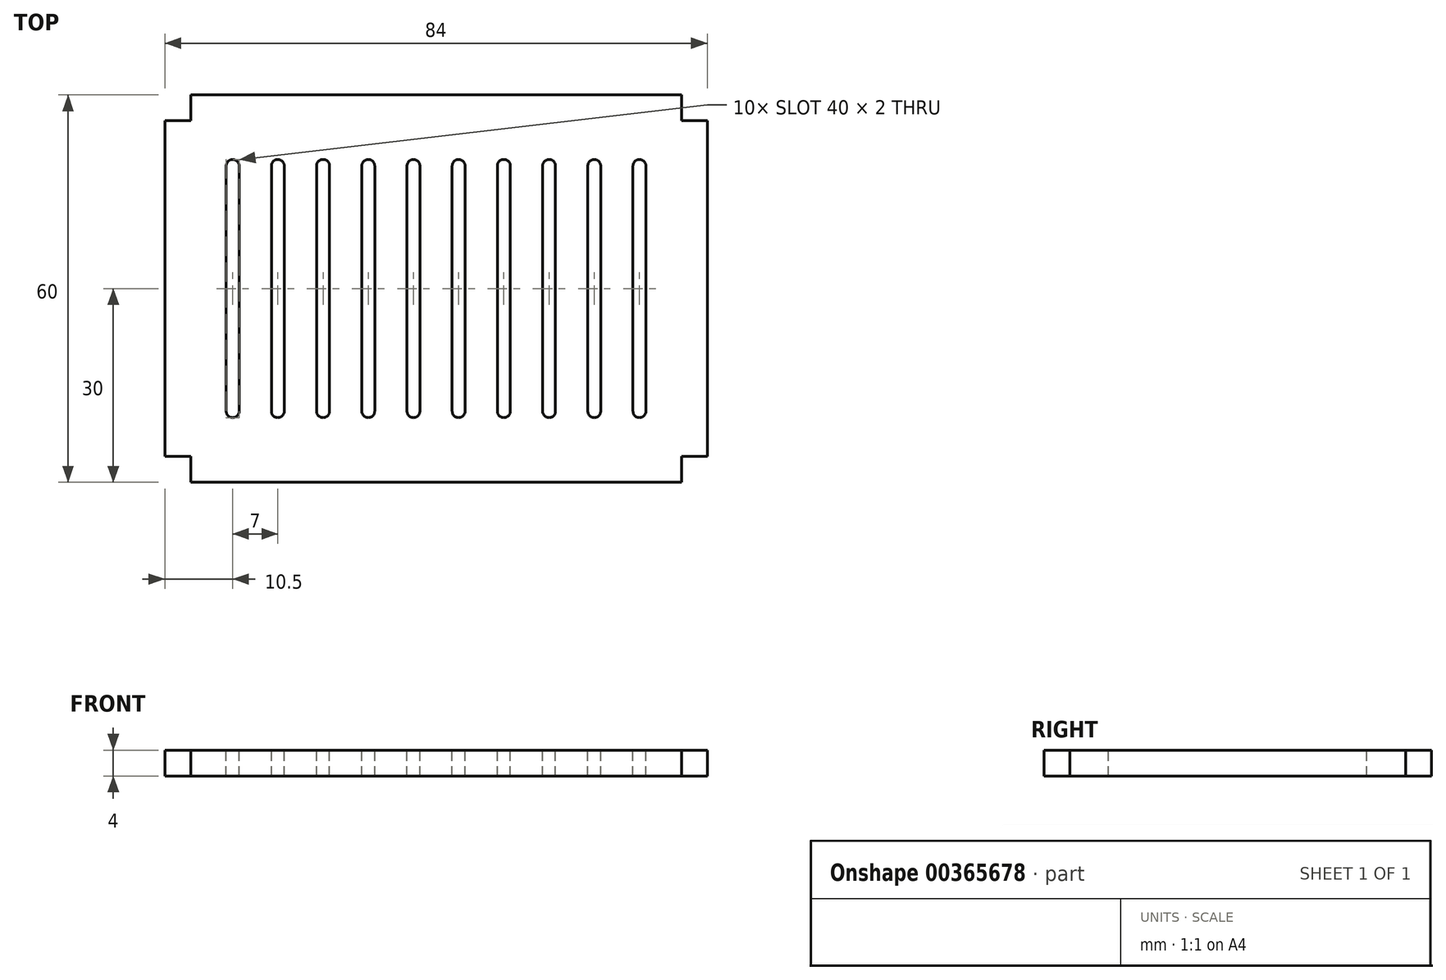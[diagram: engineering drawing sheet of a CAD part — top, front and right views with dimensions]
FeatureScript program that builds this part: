
annotation { "Feature Type Name" : "Feature", "Feature Type Description" : "" }
export const myFeature = defineFeature(function(context is Context, id is Id, definition is map)
    precondition{}
    {
        {
            var Q0;
            Q0=qCreatedBy(makeId("Top.planeOp"),FACE);
            var sketch = newSketch(context, id + "F0", { "sketchPlane" : qUnion([Q0])});
            skLineSegment(sketch, "E0.bottom", {"start": v(0, 0) * mm, "end": v(84, 0) * mm});
            skLineSegment(sketch, "E0.top", {"start": v(0, 60) * mm, "end": v(84, 60) * mm});
            skLineSegment(sketch, "E0.left", {"start": v(0, 0) * mm, "end": v(0, 60) * mm});
            skLineSegment(sketch, "E0.right", {"start": v(84, 0) * mm, "end": v(84, 60) * mm});
            skSolve(sketch);
        }
        {
            var Q0;
            Q0 = qSketchRegion(id + "F0", true);
            extrude(context, id + "F1", {"entities" : qUnion([Q0]), "depth" : 4 * mm});
        }
        {
            var Q0;
            Q0=makeQuery(id+"F1.opExtrude","CAP_FACE",FACE,{"disambiguationData":[OSD([sQuery(id+"F0.wireOp",EDGE,"E0.bottom"),sQuery(id+"F0.wireOp",EDGE,"E0.top"),sQuery(id+"F0.wireOp",EDGE,"E0.left"),sQuery(id+"F0.wireOp",EDGE,"E0.right")])],"isStart":false});
            var sketch = newSketch(context, id + "F2", { "sketchPlane" : qUnion([Q0])});
            skLineSegment(sketch, "E1.bottom", {"start": v(0, 0) * mm, "end": v(4, 0) * mm});
            skLineSegment(sketch, "E1.top", {"start": v(0, 4) * mm, "end": v(4, 4) * mm});
            skLineSegment(sketch, "E1.left", {"start": v(0, 0) * mm, "end": v(0, 4) * mm});
            skLineSegment(sketch, "E1.right", {"start": v(4, 0) * mm, "end": v(4, 4) * mm});
            skLineSegment(sketch, "E2.0.1.0", {"start": v(0, 56) * mm, "end": v(4, 56) * mm});
            skLineSegment(sketch, "E2.0.1.1", {"start": v(0, 60) * mm, "end": v(4, 60) * mm});
            skLineSegment(sketch, "E2.0.1.2", {"start": v(0, 56) * mm, "end": v(0, 60) * mm});
            skLineSegment(sketch, "E2.0.1.3", {"start": v(4, 56) * mm, "end": v(4, 60) * mm});
            skLineSegment(sketch, "E2.1.0.0", {"start": v(80, 0) * mm, "end": v(84, 0) * mm});
            skLineSegment(sketch, "E2.1.0.1", {"start": v(80, 4) * mm, "end": v(84, 4) * mm});
            skLineSegment(sketch, "E2.1.0.2", {"start": v(80, 0) * mm, "end": v(80, 4) * mm});
            skLineSegment(sketch, "E2.1.0.3", {"start": v(84, 0) * mm, "end": v(84, 4) * mm});
            skLineSegment(sketch, "E2.1.1.0", {"start": v(80, 56) * mm, "end": v(84, 56) * mm});
            skLineSegment(sketch, "E2.1.1.1", {"start": v(80, 60) * mm, "end": v(84, 60) * mm});
            skLineSegment(sketch, "E2.1.1.2", {"start": v(80, 56) * mm, "end": v(80, 60) * mm});
            skLineSegment(sketch, "E2.1.1.3", {"start": v(84, 56) * mm, "end": v(84, 60) * mm});
            skLineSegment(sketch, "E2.direction1", {"start": v(0, 0) * mm, "end": v(80, 0) * mm, "construction": true});
            skLineSegment(sketch, "E2.direction2", {"start": v(0, 0) * mm, "end": v(0, 56) * mm, "construction": true});
            skSolve(sketch);
        }
        {
            var Q0;
            Q0 = qSketchRegion(id + "F2", true);
            extrude(context, id + "F3", {"entities" : qUnion([Q0]), "operationType" : NewBodyOperationType.REMOVE, "endBound" : BoundingType.UP_TO_NEXT, "oppositeDirection" : true, "depth" : 25 * mm});
        }
        {
            var Q0;
            Q0=makeQuery(id+"F1.opExtrude","CAP_FACE",FACE,{"disambiguationData":[OSD([sQuery(id+"F0.wireOp",EDGE,"E0.bottom"),sQuery(id+"F0.wireOp",EDGE,"E0.top"),sQuery(id+"F0.wireOp",EDGE,"E0.left"),sQuery(id+"F0.wireOp",EDGE,"E0.right")])],"isStart":false});
            var sketch = newSketch(context, id + "F4", { "sketchPlane" : qUnion([Q0])});
            skLineSegment(sketch, "E3.bottom", {"start": v(10.5, 50) * mm, "end": v(10.5, 50) * mm});
            skLineSegment(sketch, "E3.top", {"start": v(10.5, 10) * mm, "end": v(10.5, 10) * mm});
            skLineSegment(sketch, "E3.left", {"start": v(9.5, 49) * mm, "end": v(9.5, 11) * mm});
            skLineSegment(sketch, "E3.right", {"start": v(11.5, 49) * mm, "end": v(11.5, 11) * mm});
            skPoint(sketch, "E4.visualSharp", {"position": v(9.5, 50) * mm});
            skArc(sketch, "E4.filletArc", {"start": v(10.5, 50) * mm, "mid": v(9.8, 49.7) * mm, "end": v(9.5, 49) * mm});
            skArc(sketch, "E5.filletArc", {"start": v(11.5, 49) * mm, "mid": v(11.2, 49.7) * mm, "end": v(10.5, 50) * mm});
            skPoint(sketch, "E6.visualSharp", {"position": v(11.5, 10) * mm});
            skArc(sketch, "E6.filletArc", {"start": v(10.5, 10) * mm, "mid": v(11.2, 10.3) * mm, "end": v(11.5, 11) * mm});
            skPoint(sketch, "E7.visualSharp", {"position": v(9.5, 10) * mm});
            skArc(sketch, "E7.filletArc", {"start": v(9.5, 11) * mm, "mid": v(9.8, 10.3) * mm, "end": v(10.5, 10) * mm});
            skPoint(sketch, "E8.1.0.0", {"position": v(16.5, 50) * mm});
            skLineSegment(sketch, "E8.1.0.1", {"start": v(16.5, 49) * mm, "end": v(16.5, 11) * mm});
            skLineSegment(sketch, "E8.1.0.2", {"start": v(18.5, 49) * mm, "end": v(18.5, 11) * mm});
            skPoint(sketch, "E8.1.0.3", {"position": v(18.5, 10) * mm});
            skPoint(sketch, "E8.1.0.4", {"position": v(16.5, 10) * mm});
            skArc(sketch, "E8.1.0.5", {"start": v(17.5, 10) * mm, "mid": v(18.2, 10.3) * mm, "end": v(18.5, 11) * mm});
            skArc(sketch, "E8.1.0.6", {"start": v(17.5, 50) * mm, "mid": v(16.8, 49.7) * mm, "end": v(16.5, 49) * mm});
            skArc(sketch, "E8.1.0.7", {"start": v(16.5, 11) * mm, "mid": v(16.8, 10.3) * mm, "end": v(17.5, 10) * mm});
            skArc(sketch, "E8.1.0.8", {"start": v(18.5, 49) * mm, "mid": v(18.2, 49.7) * mm, "end": v(17.5, 50) * mm});
            skPoint(sketch, "E8.2.0.0", {"position": v(23.5, 50) * mm});
            skLineSegment(sketch, "E8.2.0.1", {"start": v(23.5, 49) * mm, "end": v(23.5, 11) * mm});
            skLineSegment(sketch, "E8.2.0.2", {"start": v(25.5, 49) * mm, "end": v(25.5, 11) * mm});
            skPoint(sketch, "E8.2.0.3", {"position": v(25.5, 10) * mm});
            skPoint(sketch, "E8.2.0.4", {"position": v(23.5, 10) * mm});
            skArc(sketch, "E8.2.0.5", {"start": v(24.5, 10) * mm, "mid": v(25.2, 10.3) * mm, "end": v(25.5, 11) * mm});
            skArc(sketch, "E8.2.0.6", {"start": v(24.5, 50) * mm, "mid": v(23.8, 49.7) * mm, "end": v(23.5, 49) * mm});
            skArc(sketch, "E8.2.0.7", {"start": v(23.5, 11) * mm, "mid": v(23.8, 10.3) * mm, "end": v(24.5, 10) * mm});
            skArc(sketch, "E8.2.0.8", {"start": v(25.5, 49) * mm, "mid": v(25.2, 49.7) * mm, "end": v(24.5, 50) * mm});
            skPoint(sketch, "E8.3.0.0", {"position": v(30.5, 50) * mm});
            skLineSegment(sketch, "E8.3.0.1", {"start": v(30.5, 49) * mm, "end": v(30.5, 11) * mm});
            skLineSegment(sketch, "E8.3.0.2", {"start": v(32.5, 49) * mm, "end": v(32.5, 11) * mm});
            skPoint(sketch, "E8.3.0.3", {"position": v(32.5, 10) * mm});
            skPoint(sketch, "E8.3.0.4", {"position": v(30.5, 10) * mm});
            skArc(sketch, "E8.3.0.5", {"start": v(31.5, 10) * mm, "mid": v(32.2, 10.3) * mm, "end": v(32.5, 11) * mm});
            skArc(sketch, "E8.3.0.6", {"start": v(31.5, 50) * mm, "mid": v(30.8, 49.7) * mm, "end": v(30.5, 49) * mm});
            skArc(sketch, "E8.3.0.7", {"start": v(30.5, 11) * mm, "mid": v(30.8, 10.3) * mm, "end": v(31.5, 10) * mm});
            skArc(sketch, "E8.3.0.8", {"start": v(32.5, 49) * mm, "mid": v(32.2, 49.7) * mm, "end": v(31.5, 50) * mm});
            skPoint(sketch, "E8.4.0.0", {"position": v(37.5, 50) * mm});
            skLineSegment(sketch, "E8.4.0.1", {"start": v(37.5, 49) * mm, "end": v(37.5, 11) * mm});
            skLineSegment(sketch, "E8.4.0.2", {"start": v(39.5, 49) * mm, "end": v(39.5, 11) * mm});
            skPoint(sketch, "E8.4.0.3", {"position": v(39.5, 10) * mm});
            skPoint(sketch, "E8.4.0.4", {"position": v(37.5, 10) * mm});
            skArc(sketch, "E8.4.0.5", {"start": v(38.5, 10) * mm, "mid": v(39.2, 10.3) * mm, "end": v(39.5, 11) * mm});
            skArc(sketch, "E8.4.0.6", {"start": v(38.5, 50) * mm, "mid": v(37.8, 49.7) * mm, "end": v(37.5, 49) * mm});
            skArc(sketch, "E8.4.0.7", {"start": v(37.5, 11) * mm, "mid": v(37.8, 10.3) * mm, "end": v(38.5, 10) * mm});
            skArc(sketch, "E8.4.0.8", {"start": v(39.5, 49) * mm, "mid": v(39.2, 49.7) * mm, "end": v(38.5, 50) * mm});
            skPoint(sketch, "E8.5.0.0", {"position": v(44.5, 50) * mm});
            skLineSegment(sketch, "E8.5.0.1", {"start": v(44.5, 49) * mm, "end": v(44.5, 11) * mm});
            skLineSegment(sketch, "E8.5.0.2", {"start": v(46.5, 49) * mm, "end": v(46.5, 11) * mm});
            skPoint(sketch, "E8.5.0.3", {"position": v(46.5, 10) * mm});
            skPoint(sketch, "E8.5.0.4", {"position": v(44.5, 10) * mm});
            skArc(sketch, "E8.5.0.5", {"start": v(45.5, 10) * mm, "mid": v(46.2, 10.3) * mm, "end": v(46.5, 11) * mm});
            skArc(sketch, "E8.5.0.6", {"start": v(45.5, 50) * mm, "mid": v(44.8, 49.7) * mm, "end": v(44.5, 49) * mm});
            skArc(sketch, "E8.5.0.7", {"start": v(44.5, 11) * mm, "mid": v(44.8, 10.3) * mm, "end": v(45.5, 10) * mm});
            skArc(sketch, "E8.5.0.8", {"start": v(46.5, 49) * mm, "mid": v(46.2, 49.7) * mm, "end": v(45.5, 50) * mm});
            skPoint(sketch, "E8.6.0.0", {"position": v(51.5, 50) * mm});
            skLineSegment(sketch, "E8.6.0.1", {"start": v(51.5, 49) * mm, "end": v(51.5, 11) * mm});
            skLineSegment(sketch, "E8.6.0.2", {"start": v(53.5, 49) * mm, "end": v(53.5, 11) * mm});
            skPoint(sketch, "E8.6.0.3", {"position": v(53.5, 10) * mm});
            skPoint(sketch, "E8.6.0.4", {"position": v(51.5, 10) * mm});
            skArc(sketch, "E8.6.0.5", {"start": v(52.5, 10) * mm, "mid": v(53.2, 10.3) * mm, "end": v(53.5, 11) * mm});
            skArc(sketch, "E8.6.0.6", {"start": v(52.5, 50) * mm, "mid": v(51.8, 49.7) * mm, "end": v(51.5, 49) * mm});
            skArc(sketch, "E8.6.0.7", {"start": v(51.5, 11) * mm, "mid": v(51.8, 10.3) * mm, "end": v(52.5, 10) * mm});
            skArc(sketch, "E8.6.0.8", {"start": v(53.5, 49) * mm, "mid": v(53.2, 49.7) * mm, "end": v(52.5, 50) * mm});
            skPoint(sketch, "E8.7.0.0", {"position": v(58.5, 50) * mm});
            skLineSegment(sketch, "E8.7.0.1", {"start": v(58.5, 49) * mm, "end": v(58.5, 11) * mm});
            skLineSegment(sketch, "E8.7.0.2", {"start": v(60.5, 49) * mm, "end": v(60.5, 11) * mm});
            skPoint(sketch, "E8.7.0.3", {"position": v(60.5, 10) * mm});
            skPoint(sketch, "E8.7.0.4", {"position": v(58.5, 10) * mm});
            skArc(sketch, "E8.7.0.5", {"start": v(59.5, 10) * mm, "mid": v(60.2, 10.3) * mm, "end": v(60.5, 11) * mm});
            skArc(sketch, "E8.7.0.6", {"start": v(59.5, 50) * mm, "mid": v(58.8, 49.7) * mm, "end": v(58.5, 49) * mm});
            skArc(sketch, "E8.7.0.7", {"start": v(58.5, 11) * mm, "mid": v(58.8, 10.3) * mm, "end": v(59.5, 10) * mm});
            skArc(sketch, "E8.7.0.8", {"start": v(60.5, 49) * mm, "mid": v(60.2, 49.7) * mm, "end": v(59.5, 50) * mm});
            skPoint(sketch, "E8.8.0.0", {"position": v(65.5, 50) * mm});
            skLineSegment(sketch, "E8.8.0.1", {"start": v(65.5, 49) * mm, "end": v(65.5, 11) * mm});
            skLineSegment(sketch, "E8.8.0.2", {"start": v(67.5, 49) * mm, "end": v(67.5, 11) * mm});
            skPoint(sketch, "E8.8.0.3", {"position": v(67.5, 10) * mm});
            skPoint(sketch, "E8.8.0.4", {"position": v(65.5, 10) * mm});
            skArc(sketch, "E8.8.0.5", {"start": v(66.5, 10) * mm, "mid": v(67.2, 10.3) * mm, "end": v(67.5, 11) * mm});
            skArc(sketch, "E8.8.0.6", {"start": v(66.5, 50) * mm, "mid": v(65.8, 49.7) * mm, "end": v(65.5, 49) * mm});
            skArc(sketch, "E8.8.0.7", {"start": v(65.5, 11) * mm, "mid": v(65.8, 10.3) * mm, "end": v(66.5, 10) * mm});
            skArc(sketch, "E8.8.0.8", {"start": v(67.5, 49) * mm, "mid": v(67.2, 49.7) * mm, "end": v(66.5, 50) * mm});
            skPoint(sketch, "E8.9.0.0", {"position": v(72.5, 50) * mm});
            skLineSegment(sketch, "E8.9.0.1", {"start": v(72.5, 49) * mm, "end": v(72.5, 11) * mm});
            skLineSegment(sketch, "E8.9.0.2", {"start": v(74.5, 49) * mm, "end": v(74.5, 11) * mm});
            skPoint(sketch, "E8.9.0.3", {"position": v(74.5, 10) * mm});
            skPoint(sketch, "E8.9.0.4", {"position": v(72.5, 10) * mm});
            skArc(sketch, "E8.9.0.5", {"start": v(73.5, 10) * mm, "mid": v(74.2, 10.3) * mm, "end": v(74.5, 11) * mm});
            skArc(sketch, "E8.9.0.6", {"start": v(73.5, 50) * mm, "mid": v(72.8, 49.7) * mm, "end": v(72.5, 49) * mm});
            skArc(sketch, "E8.9.0.7", {"start": v(72.5, 11) * mm, "mid": v(72.8, 10.3) * mm, "end": v(73.5, 10) * mm});
            skArc(sketch, "E8.9.0.8", {"start": v(74.5, 49) * mm, "mid": v(74.2, 49.7) * mm, "end": v(73.5, 50) * mm});
            skLineSegment(sketch, "E8.direction1", {"start": v(9.5, 10) * mm, "end": v(16.5, 10) * mm, "construction": true});
            skSolve(sketch);
        }
        {
            var Q0;
            Q0 = qSketchRegion(id + "F4", true);
            extrude(context, id + "F5", {"entities" : qUnion([Q0]), "operationType" : NewBodyOperationType.REMOVE, "endBound" : BoundingType.UP_TO_NEXT, "oppositeDirection" : true, "depth" : 25 * mm});
        }
    });
